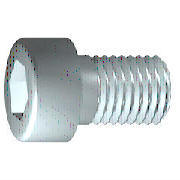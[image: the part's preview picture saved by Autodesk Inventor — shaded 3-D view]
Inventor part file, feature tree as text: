
AUTODESK INVENTOR PART (.ipt)
format: ipt  version: 2022 (Build 260153000, 153)  size: 190,976 bytes
history: native  units: mm (DEFAULTED — no unit token found)
features: sketch x2, other x1, extrude x1, plane x1, fillet x1
ambient origin geometry x7: Origin, YZ Plane, XY Plane, X Axis, Y Axis, Z Axis, Center Point
bodies: Solid1 (feature_tree)
feature tree (6):
  other  "Базовый элемент"
  extrude  "Паз"  Depth=8.8mm
  plane  "Work Plane1"
  fillet  "Fillet2"  Radius=0.24548mm
  sketch  "Эскиз1"
  sketch  "Эскиз2"
